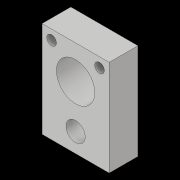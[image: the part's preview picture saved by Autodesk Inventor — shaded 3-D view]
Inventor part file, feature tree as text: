
AUTODESK INVENTOR PART (.ipt)
format: ipt  version: 2017 (Build 210142000, 142)  size: 111,616 bytes
history: native  units: in
note: dims shown in document units (in); Inventor stores cm internally (conversion verified against a paired STEP export)
features: sketch x4, extrude x3, hole x1
ambient origin geometry x8: Origin, YZ Plane, XZ Plane, XY Plane, X Axis, Y Axis, Z Axis, Center Point
bodies: Solid1 (feature_tree)
feature tree (8):
  extrude  "Extrusion1"  Depth=0.5in
  hole  "Hole1"  [1 undecoded]
  extrude  "Extrusion2"  Depth=0.1748in
  extrude  "Extrusion3"  Depth=0.1in
  sketch  "Sketch1"  dims[d0=0.35in d1=0.5in]
  sketch  "Sketch2"  dims[d2=0.15in d3=0.0in d4=0.25in]
  sketch  "Sketch3"  dims[d5=0.175in d6=0.1748in]
  sketch  "Sketch4"  dims[d7=0.2in d8=0.5in d9=0.375in d10=0.25in d11=0.5635in d12=0.75in d13=0.0in d14=0.1in d15=0.1in d16=0.175in d17=1.0in d18=0.0in d19=0.05in d20=0.05in d21=0.05in d22=0.05in d23=0.05in d24=0.05in d25=1.0in d26=0.0in]
note: 1 required parameter value undecoded (feature->parameter linkage not recoverable at this tier; creation-order binding heuristic only, values carry confidence <= 0.55)
